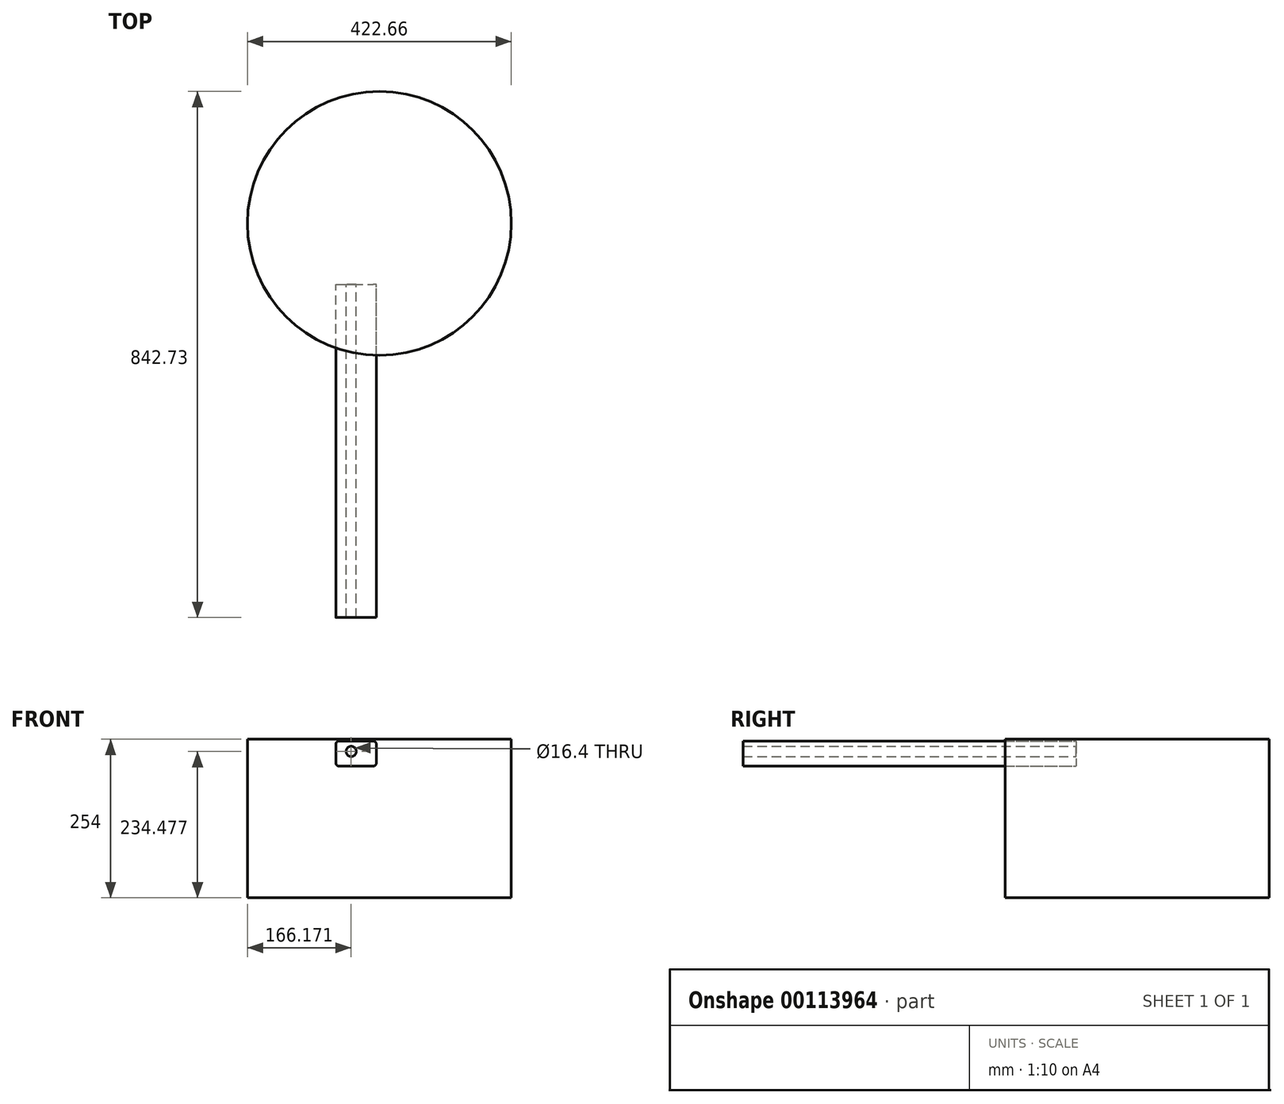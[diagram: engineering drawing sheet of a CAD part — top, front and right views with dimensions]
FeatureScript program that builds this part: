
annotation { "Feature Type Name" : "Feature", "Feature Type Description" : "" }
export const myFeature = defineFeature(function(context is Context, id is Id, definition is map)
    precondition{}
    {
        {
            var Q0;
            Q0=qCreatedBy(makeId("Front.planeOp"),FACE);
            var sketch = newSketch(context, id + "F0", { "sketchPlane" : qUnion([Q0])});
            skLineSegment(sketch, "E0.bottom", {"start": v(-69.63, -2.77) * mm, "end": v(-4.93, -2.77) * mm});
            skLineSegment(sketch, "E0.top", {"start": v(-69.63, -43.05) * mm, "end": v(-4.93, -43.05) * mm});
            skLineSegment(sketch, "E0.left", {"start": v(-69.63, -2.77) * mm, "end": v(-69.63, -43.05) * mm});
            skLineSegment(sketch, "E0.right", {"start": v(-4.93, -2.77) * mm, "end": v(-4.93, -43.05) * mm});
            skCircle(sketch, "E1", {"center": v(-45.16, -19.52) * mm, "radius": 8.2 * mm});
            skSolve(sketch);
        }
        {
            var Q0;
            Q0=makeQuery(id+"F0.imprint","IMPRINT",FACE,{"disambiguationData":[TD([[makeQuery(id+"F0.imprint","IMPRINT",EDGE,{"derivedFrom":sQuery(id+"F0.wireOp",EDGE,"E0.bottom")}),-1.0]])]});
            var Q1;
            Q1=makeQuery(id+"F0.imprint","IMPRINT",FACE,{"disambiguationData":[TD([[makeQuery(id+"F0.imprint","IMPRINT",EDGE,{"derivedFrom":sQuery(id+"F0.wireOp",EDGE,"56z93Gvd-dbOP-GdxW-tbjf-hLkYSrG7xsOT.bottom")}),-1.0]])]});
            extrude(context, id + "F1", {"entities" : qUnion([Q0, Q1]), "depth" : 533.4 * mm});
        }
        {
            var Q0;
            Q0=makeQuery(id+"F1.opExtrude","SWEPT_EDGE",EDGE,{"disambiguationData":[OSD([sQuery(id+"F0.wireOp",EDGE,"E0.bottom"),sQuery(id+"F0.wireOp",EDGE,"E0.right")])]});
            var Q1;
            Q1=makeQuery(id+"F1.opExtrude","SWEPT_EDGE",EDGE,{"disambiguationData":[OSD([sQuery(id+"F0.wireOp",EDGE,"E0.top"),sQuery(id+"F0.wireOp",EDGE,"E0.right")])]});
            var Q2;
            Q2=makeQuery(id+"F1.opExtrude","SWEPT_EDGE",EDGE,{"disambiguationData":[OSD([sQuery(id+"F0.wireOp",EDGE,"E0.bottom"),sQuery(id+"F0.wireOp",EDGE,"E0.left")])]});
            var Q3;
            Q3=makeQuery(id+"F1.opExtrude","SWEPT_EDGE",EDGE,{"disambiguationData":[OSD([sQuery(id+"F0.wireOp",EDGE,"E0.top"),sQuery(id+"F0.wireOp",EDGE,"E0.left")])]});
            fillet(context, id + "F2", {"entities" : qUnion([Q0, Q1, Q2, Q3]), "radius" : 5.08 * mm, "tangentPropagation" : true, "allowEdgeOverflow" : false});
        }
        {
            var Q0;
            Q0=qCreatedBy(makeId("Top.planeOp"),FACE);
            var sketch = newSketch(context, id + "F3", { "sketchPlane" : qUnion([Q0])});
            skCircle(sketch, "E2", {"center": v(0, 98) * mm, "radius": 211.33 * mm});
            skSolve(sketch);
        }
        {
            var Q0;
            Q0=makeQuery(id+"F3.imprint","IMPRINT",FACE,{"disambiguationData":[TD([[makeQuery(id+"F3.imprint","IMPRINT",EDGE,{"derivedFrom":sQuery(id+"F3.wireOp",EDGE,"E2")}),1.0]])]});
            extrude(context, id + "F4", {"entities" : qUnion([Q0]), "oppositeDirection" : true, "depth" : 254 * mm});
        }
    });
